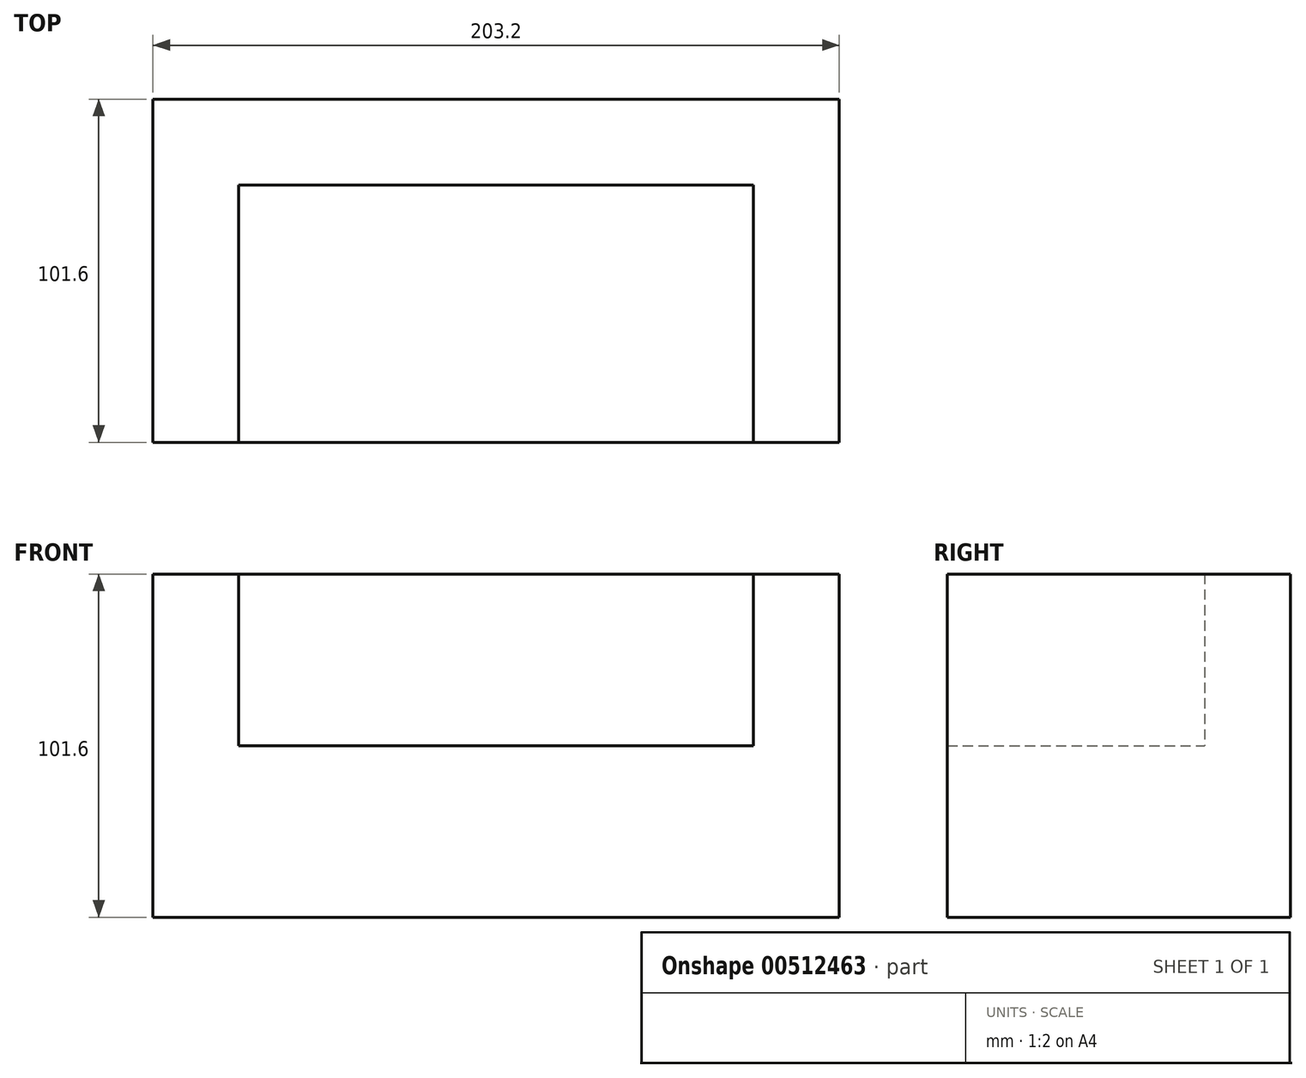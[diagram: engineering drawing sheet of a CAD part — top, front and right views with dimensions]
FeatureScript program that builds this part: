
annotation { "Feature Type Name" : "Feature", "Feature Type Description" : "" }
export const myFeature = defineFeature(function(context is Context, id is Id, definition is map)
    precondition{}
    {
        {
            var Q0;
            Q0=qCreatedBy(makeId("Front.planeOp"),FACE);
            var sketch = newSketch(context, id + "F0", { "sketchPlane" : qUnion([Q0])});
            skLineSegment(sketch, "E0.bottom", {"start": v(0, 0) * mm, "end": v(203.2, 0) * mm});
            skLineSegment(sketch, "E0.top", {"start": v(0, 50.8) * mm, "end": v(203.2, 50.8) * mm});
            skLineSegment(sketch, "E0.left", {"start": v(0, 0) * mm, "end": v(0, 50.8) * mm});
            skLineSegment(sketch, "E0.right", {"start": v(203.2, 0) * mm, "end": v(203.2, 50.8) * mm});
            skSolve(sketch);
        }
        {
            var Q0;
            Q0=makeQuery(id+"F0.imprint","IMPRINT",FACE,{"disambiguationData":[TD([[makeQuery(id+"F0.imprint","IMPRINT",EDGE,{"derivedFrom":sQuery(id+"F0.wireOp",EDGE,"E0.bottom")}),1.0]])]});
            extrude(context, id + "F1", {"entities" : qUnion([Q0]), "depth" : 101.6 * mm});
        }
        {
            var Q0;
            Q0=makeQuery(id+"F1.opExtrude","SWEPT_FACE",FACE,{"disambiguationData":[OSD([sQuery(id+"F0.wireOp",EDGE,"E0.top")])]});
            var sketch = newSketch(context, id + "F2", { "sketchPlane" : qUnion([Q0])});
            skLineSegment(sketch, "E1.bottom", {"start": v(0, 0) * mm, "end": v(203.2, 0) * mm});
            skLineSegment(sketch, "E1.top", {"start": v(0, -25.4) * mm, "end": v(203.2, -25.4) * mm});
            skLineSegment(sketch, "E1.left", {"start": v(0, 0) * mm, "end": v(0, -25.4) * mm});
            skLineSegment(sketch, "E1.right", {"start": v(203.2, 0) * mm, "end": v(203.2, -25.4) * mm});
            skSolve(sketch);
        }
        {
            var Q0;
            Q0=makeQuery(id+"F2.imprint","IMPRINT",FACE,{"disambiguationData":[TD([[makeQuery(id+"F2.imprint","IMPRINT",EDGE,{"derivedFrom":sQuery(id+"F2.wireOp",EDGE,"E1.bottom")}),-1.0]])]});
            extrude(context, id + "F3", {"entities" : qUnion([Q0]), "operationType" : NewBodyOperationType.ADD, "depth" : 50.8 * mm});
        }
        {
            var Q0;
            Q0=makeQuery(id+"F1.opExtrude","SWEPT_FACE",FACE,{"disambiguationData":[OSD([sQuery(id+"F0.wireOp",EDGE,"E0.top")])]});
            var sketch = newSketch(context, id + "F4", { "sketchPlane" : qUnion([Q0])});
            skLineSegment(sketch, "E2.bottom", {"start": v(0, -101.6) * mm, "end": v(25.4, -101.6) * mm});
            skLineSegment(sketch, "E2.top", {"start": v(0, -25.4) * mm, "end": v(25.4, -25.4) * mm});
            skLineSegment(sketch, "E2.left", {"start": v(0, -101.6) * mm, "end": v(0, -25.4) * mm});
            skLineSegment(sketch, "E2.right", {"start": v(25.4, -101.6) * mm, "end": v(25.4, -25.4) * mm});
            skSolve(sketch);
        }
        {
            var Q0;
            Q0=makeQuery(id+"F4.imprint","IMPRINT",FACE,{"disambiguationData":[TD([[makeQuery(id+"F4.imprint","IMPRINT",EDGE,{"derivedFrom":sQuery(id+"F4.wireOp",EDGE,"E2.bottom")}),1.0]])]});
            extrude(context, id + "F5", {"entities" : qUnion([Q0]), "operationType" : NewBodyOperationType.ADD, "depth" : 50.8 * mm});
        }
        {
            var Q0;
            Q0=makeQuery(id+"F1.opExtrude","SWEPT_FACE",FACE,{"disambiguationData":[OSD([sQuery(id+"F0.wireOp",EDGE,"E0.top")])]});
            var sketch = newSketch(context, id + "F6", { "sketchPlane" : qUnion([Q0])});
            skLineSegment(sketch, "E3.bottom", {"start": v(203.2, -101.6) * mm, "end": v(177.8, -101.6) * mm});
            skLineSegment(sketch, "E3.top", {"start": v(203.2, -25.4) * mm, "end": v(177.8, -25.4) * mm});
            skLineSegment(sketch, "E3.left", {"start": v(203.2, -101.6) * mm, "end": v(203.2, -25.4) * mm});
            skLineSegment(sketch, "E3.right", {"start": v(177.8, -101.6) * mm, "end": v(177.8, -25.4) * mm});
            skSolve(sketch);
        }
        {
            var Q0;
            Q0=makeQuery(id+"F6.imprint","IMPRINT",FACE,{"disambiguationData":[TD([[makeQuery(id+"F6.imprint","IMPRINT",EDGE,{"derivedFrom":sQuery(id+"F6.wireOp",EDGE,"E3.bottom")}),1.0]])]});
            extrude(context, id + "F7", {"entities" : qUnion([Q0]), "operationType" : NewBodyOperationType.ADD, "depth" : 50.8 * mm});
        }
    });
